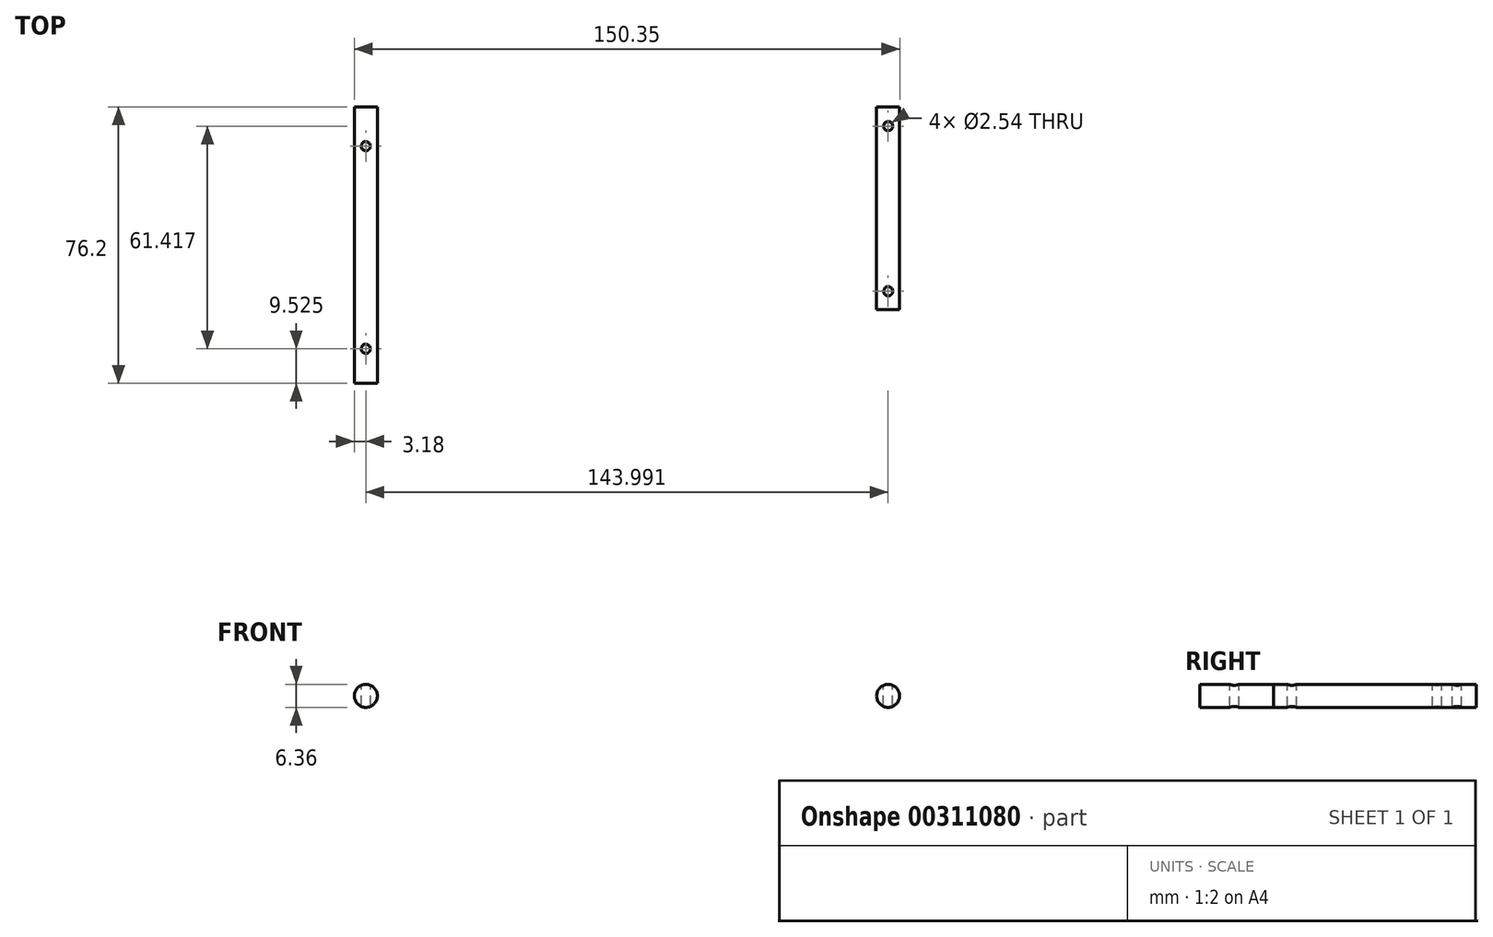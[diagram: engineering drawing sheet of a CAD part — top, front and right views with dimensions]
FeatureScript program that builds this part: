
annotation { "Feature Type Name" : "Feature", "Feature Type Description" : "" }
export const myFeature = defineFeature(function(context is Context, id is Id, definition is map)
    precondition{}
    {
        {
            var Q0;
            Q0=qCreatedBy(makeId("Front.planeOp"),FACE);
            var sketch = newSketch(context, id + "F0", { "sketchPlane" : qUnion([Q0])});
            skCircle(sketch, "E0", {"center": v(0, 0) * mm, "radius": 3.18 * mm});
            skCircle(sketch, "E1", {"center": v(144, 0) * mm, "radius": 3.18 * mm});
            skSolve(sketch);
        }
        {
            var Q0;
            Q0=makeQuery(id+"F0.imprint","IMPRINT",FACE,{"disambiguationData":[TD([[makeQuery(id+"F0.imprint","IMPRINT",EDGE,{"derivedFrom":sQuery(id+"F0.wireOp",EDGE,"E0")}),1.0]])]});
            extrude(context, id + "F1", {"entities" : qUnion([Q0]), "depth" : 76.2 * mm});
        }
        {
            var Q0;
            Q0=makeQuery(id+"F0.imprint","IMPRINT",FACE,{"disambiguationData":[TD([[makeQuery(id+"F0.imprint","IMPRINT",EDGE,{"derivedFrom":sQuery(id+"F0.wireOp",EDGE,"E1")}),1.0]])]});
            extrude(context, id + "F2", {"entities" : qUnion([Q0]), "depth" : 55.88 * mm});
        }
        {
            var Q0;
            Q0=qCreatedBy(makeId("Top.planeOp"),FACE);
            cPlane(context, id + "F3", {"entities" : qUnion([Q0]), "cplaneType" : CPlaneType.OFFSET, "offset" : 3.8 * mm, "width" : 152.4 * mm, "height" : 152.4 * mm});
        }
        {
            var Q0;
            Q0=qCreatedBy(id+"F3.planeOp",FACE);
            var sketch = newSketch(context, id + "F4", { "sketchPlane" : qUnion([Q0])});
            skCircle(sketch, "E2", {"center": v(0, -10.8) * mm, "radius": 1.27 * mm});
            skCircle(sketch, "E3", {"center": v(0, -66.68) * mm, "radius": 1.27 * mm});
            skLineSegment(sketch, "E4.0", {"start": v(147.17, 0) * mm, "end": v(140.82, 0) * mm});
            skLineSegment(sketch, "E5.0", {"start": v(147.17, -55.88) * mm, "end": v(140.82, -55.88) * mm});
            skCircle(sketch, "E6", {"center": v(144, -5.26) * mm, "radius": 1.27 * mm});
            skPoint(sketch, "E6.centerSnap0", {"position": v(144, 0) * mm});
            skCircle(sketch, "E7", {"center": v(144, -50.8) * mm, "radius": 1.27 * mm});
            skSolve(sketch);
        }
        {
            var Q0;
            Q0=makeQuery(id+"F4.imprint","IMPRINT",FACE,{"disambiguationData":[TD([[makeQuery(id+"F4.imprint","IMPRINT",EDGE,{"derivedFrom":sQuery(id+"F4.wireOp",EDGE,"E3")}),1.0]])]});
            var Q1;
            Q1=makeQuery(id+"F4.imprint","IMPRINT",FACE,{"disambiguationData":[TD([[makeQuery(id+"F4.imprint","IMPRINT",EDGE,{"derivedFrom":sQuery(id+"F4.wireOp",EDGE,"E2")}),1.0]])]});
            var Q2;
            Q2=makeQuery(id+"F4.imprint","IMPRINT",FACE,{"disambiguationData":[TD([[makeQuery(id+"F4.imprint","IMPRINT",EDGE,{"derivedFrom":sQuery(id+"F4.wireOp",EDGE,"E7")}),1.0]])]});
            var Q3;
            Q3=makeQuery(id+"F4.imprint","IMPRINT",FACE,{"disambiguationData":[TD([[makeQuery(id+"F4.imprint","IMPRINT",EDGE,{"derivedFrom":sQuery(id+"F4.wireOp",EDGE,"E6")}),1.0]])]});
            extrude(context, id + "F5", {"entities" : qUnion([Q0, Q1, Q2, Q3]), "operationType" : NewBodyOperationType.REMOVE, "oppositeDirection" : true, "depth" : 25.4 * mm});
        }
    });
